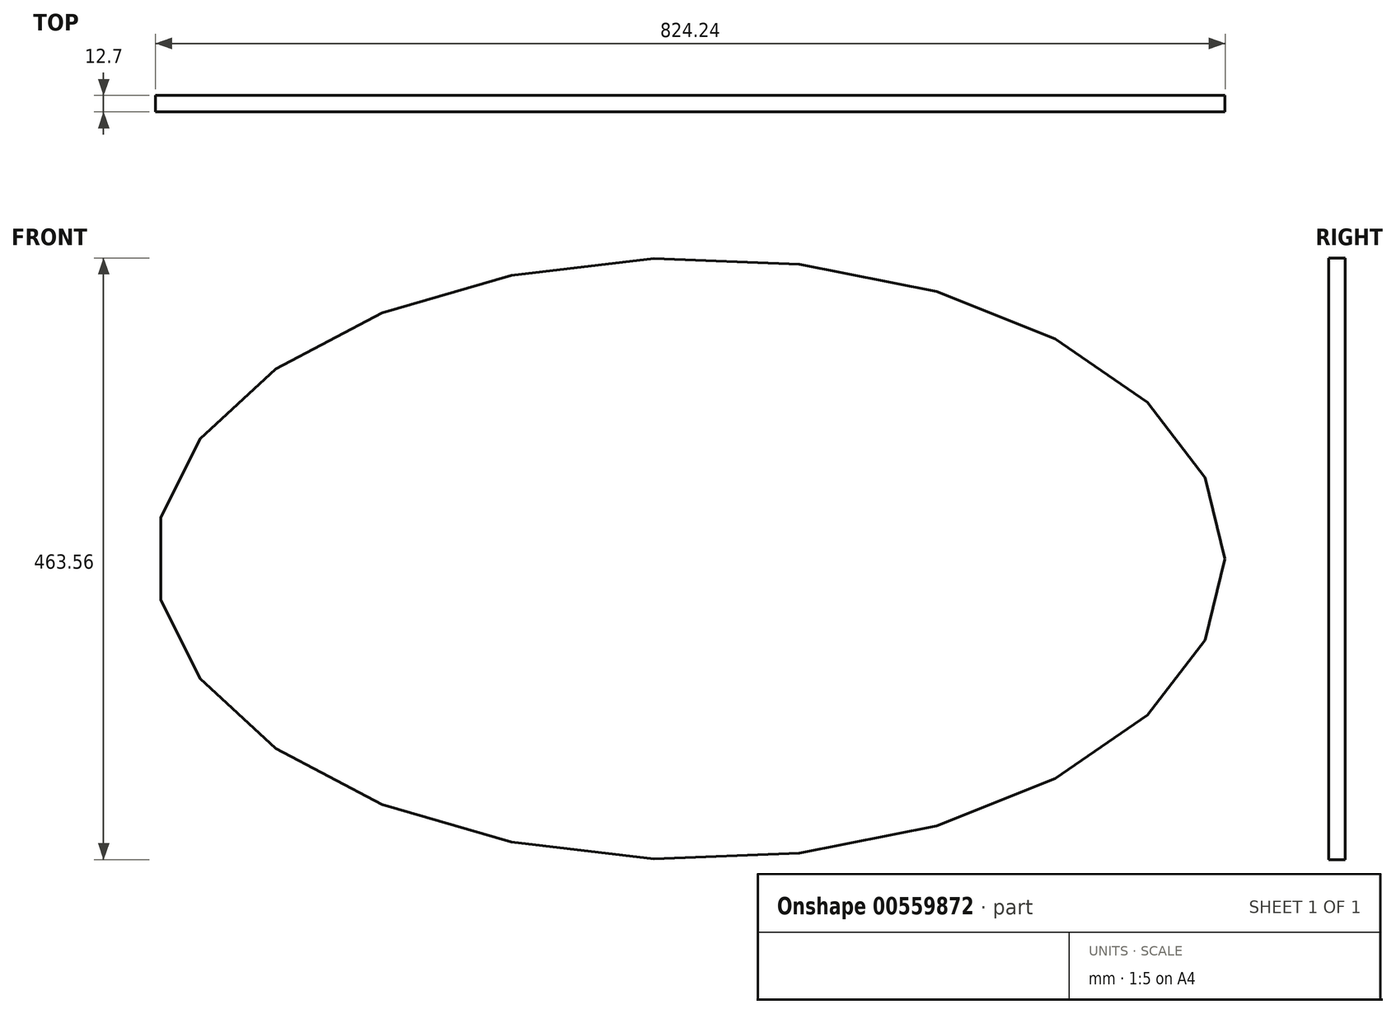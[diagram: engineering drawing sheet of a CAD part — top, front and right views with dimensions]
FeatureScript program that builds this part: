
annotation { "Feature Type Name" : "Feature", "Feature Type Description" : "" }
export const myFeature = defineFeature(function(context is Context, id is Id, definition is map)
    precondition{}
    {
        {
            var Q0;
            Q0=qCreatedBy(makeId("Front.planeOp"),FACE);
            var sketch = newSketch(context, id + "F0", { "sketchPlane" : qUnion([Q0])});
            skEllipse(sketch, "E0", {"center": v(0, 0) * mm, "majorRadius": 412.12 * mm, "minorRadius": 231.78 * mm, "majorAxis": v(1, 0)});
            skSolve(sketch);
        }
        {
            var Q0;
            Q0=makeQuery(id+"F0.imprint","IMPRINT",FACE,{"disambiguationData":[TD([[makeQuery(id+"F0.imprint","IMPRINT",EDGE,{"derivedFrom":sQuery(id+"F0.wireOp",EDGE,"E0")}),1.0]])]});
            extrude(context, id + "F1", {"entities" : qUnion([Q0]), "depth" : 12.7 * mm, "offsetDistance" : 25.4 * mm});
        }
    });
